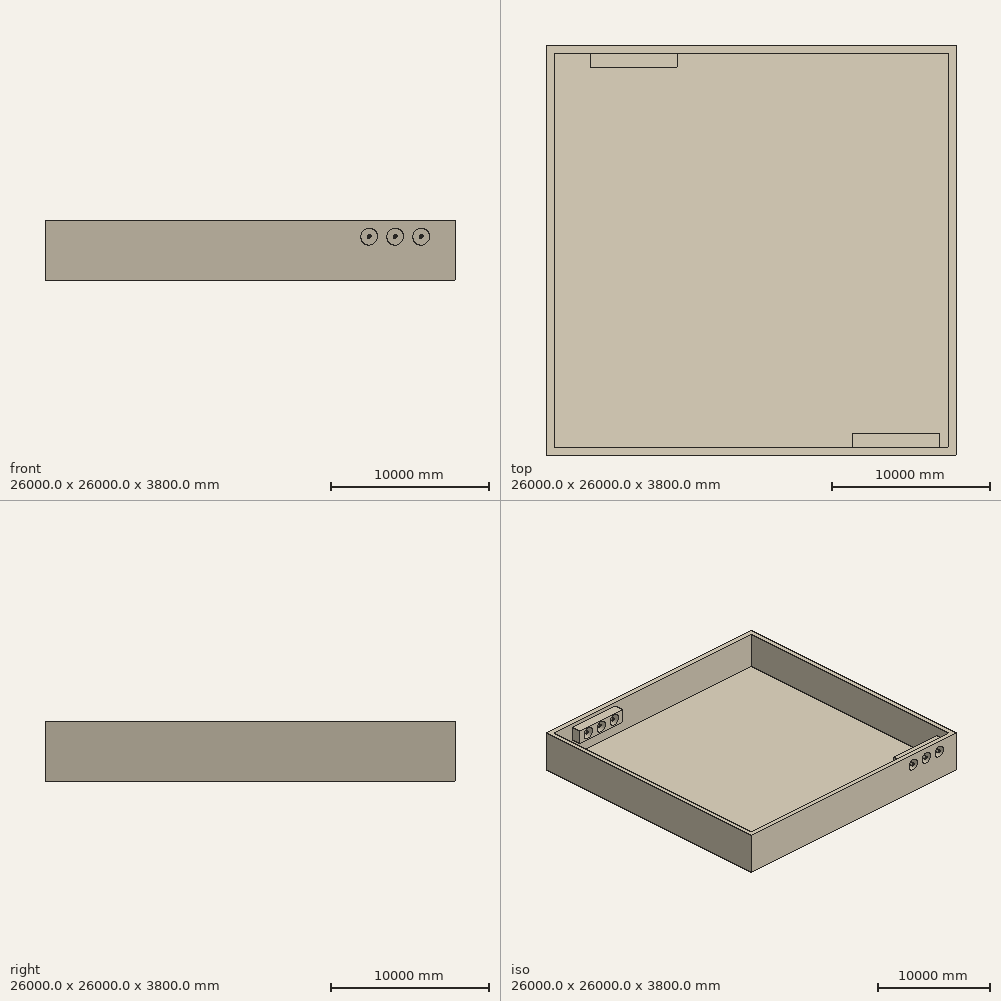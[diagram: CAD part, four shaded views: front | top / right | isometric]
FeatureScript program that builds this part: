
annotation { "Feature Type Name" : "Feature", "Feature Type Description" : "" }
export const myFeature = defineFeature(function(context is Context, id is Id, definition is map)
    precondition{}
    {
        {
            var Q0;
            Q0=qCreatedBy(makeId("Top.planeOp"),FACE);
            var sketch = newSketch(context, id + "F0", { "sketchPlane" : qUnion([Q0])});
            skLineSegment(sketch, "E0.bottom", {"start": v(-13000, 13000) * mm, "end": v(13000, 13000) * mm});
            skLineSegment(sketch, "E0.top", {"start": v(-13000, -13000) * mm, "end": v(13000, -13000) * mm});
            skLineSegment(sketch, "E0.left", {"start": v(-13000, 13000) * mm, "end": v(-13000, -13000) * mm});
            skLineSegment(sketch, "E0.right", {"start": v(13000, 13000) * mm, "end": v(13000, -13000) * mm});
            skLineSegment(sketch, "E1.bottom", {"start": v(-12510, 12510) * mm, "end": v(12510, 12510) * mm});
            skLineSegment(sketch, "E1.top", {"start": v(-12510, -12510) * mm, "end": v(12510, -12510) * mm});
            skLineSegment(sketch, "E1.left", {"start": v(-12510, 12510) * mm, "end": v(-12510, -12510) * mm});
            skLineSegment(sketch, "E1.right", {"start": v(12510, 12510) * mm, "end": v(12510, -12510) * mm});
            skSolve(sketch);
        }
        {
            var Q0;
            Q0=makeQuery(id+"F0.imprint","IMPRINT",FACE,{"disambiguationData":[TD([[makeQuery(id+"F0.imprint","IMPRINT",EDGE,{"derivedFrom":sQuery(id+"F0.wireOp",EDGE,"E0.bottom")}),-1.0]])]});
            extrude(context, id + "F1", {"entities" : qUnion([Q0]), "depth" : 3800 * mm, "offsetDistance" : 25.4 * mm});
        }
        {
            var Q0;
            Q0=qCreatedBy(makeId("Top.planeOp"),FACE);
            var sketch = newSketch(context, id + "F2", { "sketchPlane" : qUnion([Q0])});
            skLineSegment(sketch, "E2.bottom", {"start": v(-12510, 12510) * mm, "end": v(12510, 12510) * mm});
            skLineSegment(sketch, "E2.top", {"start": v(-12510, -12510) * mm, "end": v(12510, -12510) * mm});
            skLineSegment(sketch, "E2.left", {"start": v(-12510, 12510) * mm, "end": v(-12510, -12510) * mm});
            skLineSegment(sketch, "E2.right", {"start": v(12510, 12510) * mm, "end": v(12510, -12510) * mm});
            skSolve(sketch);
        }
        {
            var Q0;
            Q0=qSketchRegion(id+"F2",true);
            extrude(context, id + "F3", {"entities" : qUnion([Q0]), "operationType" : NewBodyOperationType.ADD, "depth" : 490 * mm, "offsetDistance" : 25.4 * mm});
        }
        {
            var Q0;
            Q0=makeQuery(id+"F1.opExtrude","SWEPT_FACE",FACE,{"disambiguationData":[OSD([sQuery(id+"F0.wireOp",EDGE,"E1.bottom")])]});
            var sketch = newSketch(context, id + "F4", { "sketchPlane" : qUnion([Q0])});
            skLineSegment(sketch, "E3.bottom", {"start": v(-10188.17, 3419) * mm, "end": v(-4688.17, 3419) * mm});
            skLineSegment(sketch, "E3.top", {"start": v(-10188.17, 2119) * mm, "end": v(-4688.17, 2119) * mm});
            skLineSegment(sketch, "E3.left", {"start": v(-10188.17, 3419) * mm, "end": v(-10188.17, 2119) * mm});
            skLineSegment(sketch, "E3.right", {"start": v(-4688.17, 3419) * mm, "end": v(-4688.17, 2119) * mm});
            skSolve(sketch);
        }
        {
            var Q0;
            Q0=makeQuery(id+"F4.imprint","IMPRINT",FACE,{"disambiguationData":[TD([[makeQuery(id+"F4.imprint","IMPRINT",EDGE,{"derivedFrom":sQuery(id+"F4.wireOp",EDGE,"E3.bottom")}),-1.0]])]});
            extrude(context, id + "F5", {"entities" : qUnion([Q0]), "operationType" : NewBodyOperationType.ADD, "depth" : 900 * mm, "offsetDistance" : 25.4 * mm});
        }
        {
            var Q0;
            Q0=makeQuery(id+"F5.opExtrude","CAP_FACE",FACE,{"disambiguationData":[OSD([sQuery(id+"F4.wireOp",EDGE,"E3.bottom"),sQuery(id+"F4.wireOp",EDGE,"E3.top"),sQuery(id+"F4.wireOp",EDGE,"E3.left"),sQuery(id+"F4.wireOp",EDGE,"E3.right")])],"isStart":false});
            var sketch = newSketch(context, id + "F6", { "sketchPlane" : qUnion([Q0])});
            skCircle(sketch, "E4", {"center": v(-7438.17, 2769) * mm, "radius": 533.4 * mm});
            skPoint(sketch, "E4.centerSnap0", {"position": v(-7438.17, 2119) * mm});
            skCircle(sketch, "E5", {"center": v(-9089.17, 2769) * mm, "radius": 533.4 * mm});
            skCircle(sketch, "E6", {"center": v(-5787.17, 2769) * mm, "radius": 533.4 * mm});
            skSolve(sketch);
        }
        {
            var Q0;
            Q0=makeQuery(id+"F6.imprint","IMPRINT",FACE,{"disambiguationData":[TD([[makeQuery(id+"F6.imprint","IMPRINT",EDGE,{"derivedFrom":sQuery(id+"F6.wireOp",EDGE,"E5")}),1.0]])]});
            var Q1;
            Q1=makeQuery(id+"F6.imprint","IMPRINT",FACE,{"disambiguationData":[TD([[makeQuery(id+"F6.imprint","IMPRINT",EDGE,{"derivedFrom":sQuery(id+"F6.wireOp",EDGE,"E4")}),1.0]])]});
            var Q2;
            Q2=makeQuery(id+"F6.imprint","IMPRINT",FACE,{"disambiguationData":[TD([[makeQuery(id+"F6.imprint","IMPRINT",EDGE,{"derivedFrom":sQuery(id+"F6.wireOp",EDGE,"E6")}),1.0]])]});
            extrude(context, id + "F7", {"entities" : qUnion([Q0, Q1, Q2]), "operationType" : NewBodyOperationType.REMOVE, "endBound" : BoundingType.UP_TO_NEXT, "oppositeDirection" : true, "depth" : 25.4 * mm, "offsetDistance" : 25.4 * mm});
        }
        {
            var Q0;
            Q0=makeQuery(id+"F1.opExtrude","SWEPT_FACE",FACE,{"disambiguationData":[OSD([sQuery(id+"F0.wireOp",EDGE,"E0.bottom")])]});
            var sketch = newSketch(context, id + "F8", { "sketchPlane" : qUnion([Q0])});
            skCircle(sketch, "E7", {"center": v(9089.17, 2769) * mm, "radius": 127 * mm});
            skCircle(sketch, "E8", {"center": v(9089.17, 2769) * mm, "radius": 63.5 * mm});
            skCircle(sketch, "E9", {"center": v(7438.17, 2769) * mm, "radius": 127 * mm});
            skCircle(sketch, "E10", {"center": v(7438.17, 2769) * mm, "radius": 63.5 * mm});
            skCircle(sketch, "E11", {"center": v(5787.17, 2769) * mm, "radius": 127 * mm});
            skCircle(sketch, "E12", {"center": v(5787.17, 2769) * mm, "radius": 63.5 * mm});
            skSolve(sketch);
        }
        {
            var Q0;
            Q0=makeQuery(id+"F8.imprint","IMPRINT",FACE,{"disambiguationData":[TD([[makeQuery(id+"F8.imprint","IMPRINT",EDGE,{"derivedFrom":sQuery(id+"F8.wireOp",EDGE,"E11")}),1.0]])]});
            var Q1;
            Q1=makeQuery(id+"F8.imprint","IMPRINT",FACE,{"disambiguationData":[TD([[makeQuery(id+"F8.imprint","IMPRINT",EDGE,{"derivedFrom":sQuery(id+"F8.wireOp",EDGE,"E9")}),1.0]])]});
            var Q2;
            Q2=makeQuery(id+"F8.imprint","IMPRINT",FACE,{"disambiguationData":[TD([[makeQuery(id+"F8.imprint","IMPRINT",EDGE,{"derivedFrom":sQuery(id+"F8.wireOp",EDGE,"E7")}),1.0]])]});
            extrude(context, id + "F9", {"entities" : qUnion([Q0, Q1, Q2]), "oppositeDirection" : true, "depth" : 1270 * mm, "offsetDistance" : 25.4 * mm});
        }
        {
            var Q0;
            Q0=makeQuery(id+"F1.opExtrude","SWEPT_FACE",FACE,{"disambiguationData":[OSD([sQuery(id+"F0.wireOp",EDGE,"E1.top")])]});
            var sketch = newSketch(context, id + "F10", { "sketchPlane" : qUnion([Q0])});
            skLineSegment(sketch, "E13.bottom", {"start": v(-11926.96, 3419) * mm, "end": v(-6426.96, 3419) * mm});
            skLineSegment(sketch, "E13.top", {"start": v(-11926.96, 2119) * mm, "end": v(-6426.96, 2119) * mm});
            skLineSegment(sketch, "E13.left", {"start": v(-11926.96, 3419) * mm, "end": v(-11926.96, 2119) * mm});
            skLineSegment(sketch, "E13.right", {"start": v(-6426.96, 3419) * mm, "end": v(-6426.96, 2119) * mm});
            skSolve(sketch);
        }
        {
            var Q0;
            Q0=makeQuery(id+"F10.imprint","IMPRINT",FACE,{"disambiguationData":[TD([[makeQuery(id+"F10.imprint","IMPRINT",EDGE,{"derivedFrom":sQuery(id+"F10.wireOp",EDGE,"E13.bottom")}),-1.0]])]});
            extrude(context, id + "F11", {"entities" : qUnion([Q0]), "operationType" : NewBodyOperationType.ADD, "depth" : 900 * mm, "offsetDistance" : 25.4 * mm});
        }
        {
            var Q0;
            Q0=makeQuery(id+"F11.opExtrude","CAP_FACE",FACE,{"disambiguationData":[OSD([sQuery(id+"F10.wireOp",EDGE,"E13.bottom"),sQuery(id+"F10.wireOp",EDGE,"E13.top"),sQuery(id+"F10.wireOp",EDGE,"E13.left"),sQuery(id+"F10.wireOp",EDGE,"E13.right")])],"isStart":false});
            var sketch = newSketch(context, id + "F12", { "sketchPlane" : qUnion([Q0])});
            skCircle(sketch, "E14", {"center": v(-9176.96, 2769) * mm, "radius": 533.4 * mm});
            skPoint(sketch, "E14.centerSnap0", {"position": v(-9176.96, 2119) * mm});
            skCircle(sketch, "E15", {"center": v(-10827.96, 2769) * mm, "radius": 533.4 * mm});
            skCircle(sketch, "E16", {"center": v(-7525.96, 2769) * mm, "radius": 533.4 * mm});
            skSolve(sketch);
        }
        {
            var Q0;
            Q0=makeQuery(id+"F12.imprint","IMPRINT",FACE,{"disambiguationData":[TD([[makeQuery(id+"F12.imprint","IMPRINT",EDGE,{"derivedFrom":sQuery(id+"F12.wireOp",EDGE,"E15")}),1.0]])]});
            var Q1;
            Q1=makeQuery(id+"F12.imprint","IMPRINT",FACE,{"disambiguationData":[TD([[makeQuery(id+"F12.imprint","IMPRINT",EDGE,{"derivedFrom":sQuery(id+"F12.wireOp",EDGE,"E14")}),1.0]])]});
            var Q2;
            Q2=makeQuery(id+"F12.imprint","IMPRINT",FACE,{"disambiguationData":[TD([[makeQuery(id+"F12.imprint","IMPRINT",EDGE,{"derivedFrom":sQuery(id+"F12.wireOp",EDGE,"E16")}),1.0]])]});
            extrude(context, id + "F13", {"entities" : qUnion([Q0, Q1, Q2]), "operationType" : NewBodyOperationType.REMOVE, "endBound" : BoundingType.UP_TO_NEXT, "oppositeDirection" : true, "depth" : 25.4 * mm, "offsetDistance" : 25.4 * mm});
        }
        {
            var Q0;
            Q0=makeQuery(id+"F1.opExtrude","SWEPT_FACE",FACE,{"disambiguationData":[OSD([sQuery(id+"F0.wireOp",EDGE,"E0.top")])]});
            var sketch = newSketch(context, id + "F14", { "sketchPlane" : qUnion([Q0])});
            skCircle(sketch, "E17", {"center": v(10827.96, 2769) * mm, "radius": 63.5 * mm});
            skCircle(sketch, "E18", {"center": v(10827.96, 2769) * mm, "radius": 127 * mm});
            skCircle(sketch, "E19", {"center": v(9176.96, 2769) * mm, "radius": 127 * mm});
            skCircle(sketch, "E20", {"center": v(9176.96, 2769) * mm, "radius": 63.5 * mm});
            skCircle(sketch, "E21", {"center": v(7525.96, 2769) * mm, "radius": 127 * mm});
            skCircle(sketch, "E22", {"center": v(7525.96, 2769) * mm, "radius": 63.5 * mm});
            skSolve(sketch);
        }
        {
            var Q0;
            Q0=makeQuery(id+"F14.imprint","IMPRINT",FACE,{"disambiguationData":[TD([[makeQuery(id+"F14.imprint","IMPRINT",EDGE,{"derivedFrom":sQuery(id+"F14.wireOp",EDGE,"E21")}),1.0]])]});
            var Q1;
            Q1=makeQuery(id+"F14.imprint","IMPRINT",FACE,{"disambiguationData":[TD([[makeQuery(id+"F14.imprint","IMPRINT",EDGE,{"derivedFrom":sQuery(id+"F14.wireOp",EDGE,"E19")}),1.0]])]});
            var Q2;
            Q2=makeQuery(id+"F14.imprint","IMPRINT",FACE,{"disambiguationData":[TD([[makeQuery(id+"F14.imprint","IMPRINT",EDGE,{"derivedFrom":sQuery(id+"F14.wireOp",EDGE,"E17")}),-1.0]])]});
            extrude(context, id + "F15", {"entities" : qUnion([Q0, Q1, Q2]), "oppositeDirection" : true, "depth" : 1270 * mm, "offsetDistance" : 25.4 * mm});
        }
    });
